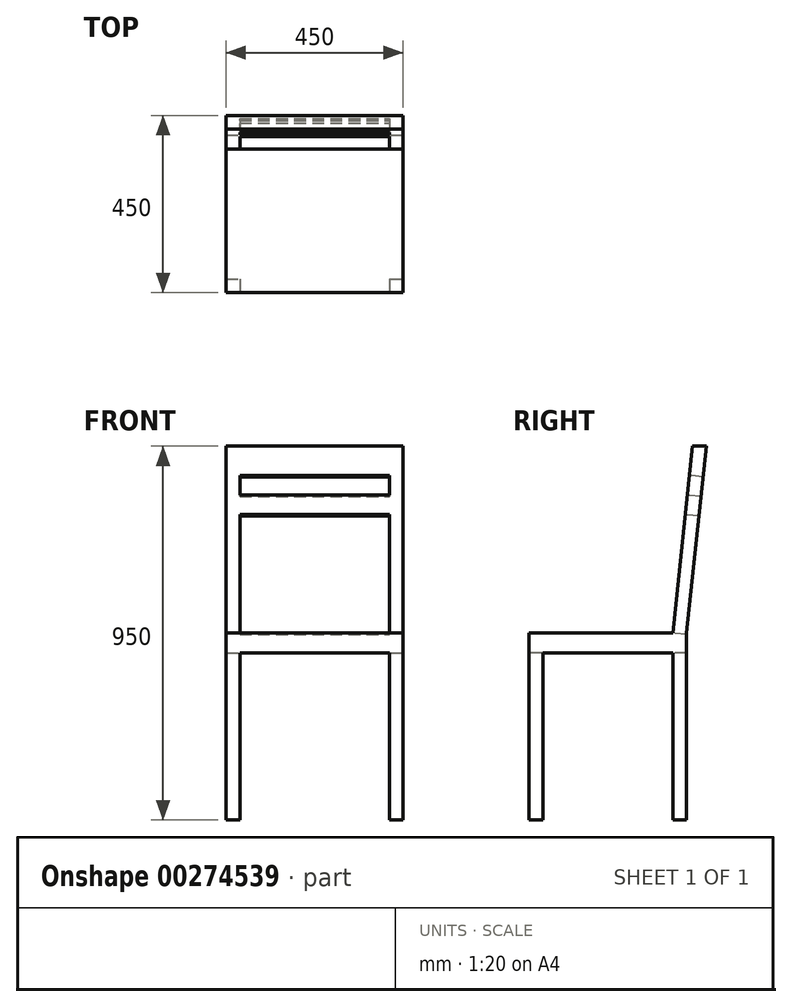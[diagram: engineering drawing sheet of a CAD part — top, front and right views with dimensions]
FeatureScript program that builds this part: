
annotation { "Feature Type Name" : "Feature", "Feature Type Description" : "" }
export const myFeature = defineFeature(function(context is Context, id is Id, definition is map)
    precondition{}
    {
        {
            var Q0;
            Q0=qCreatedBy(makeId("Top.planeOp"),FACE);
            var sketch = newSketch(context, id + "F0", { "sketchPlane" : qUnion([Q0])});
            skLineSegment(sketch, "E0.bottom", {"start": v(225, 225) * mm, "end": v(-225, 225) * mm});
            skLineSegment(sketch, "E0.top", {"start": v(225, -225) * mm, "end": v(-225, -225) * mm});
            skLineSegment(sketch, "E0.left", {"start": v(225, 225) * mm, "end": v(225, -225) * mm});
            skLineSegment(sketch, "E0.right", {"start": v(-225, 225) * mm, "end": v(-225, -225) * mm});
            skPoint(sketch, "E0.middle", {"position": v(0, 0) * mm});
            skSolve(sketch);
        }
        {
            var Q0;
            Q0=qSketchRegion(id+"F0",true);
            extrude(context, id + "F1", {"entities" : qUnion([Q0]), "depth" : 950 * mm});
        }
        {
            var Q0;
            Q0=makeQuery(id+"F1.opExtrude","SWEPT_FACE",FACE,{"disambiguationData":[OSD([sQuery(id+"F0.wireOp",EDGE,"E0.left")])]});
            var sketch = newSketch(context, id + "F2", { "sketchPlane" : qUnion([Q0])});
            skLineSegment(sketch, "E1.bottom", {"start": v(225, 475) * mm, "end": v(-225, 475) * mm});
            skLineSegment(sketch, "E1.top", {"start": v(225, 425) * mm, "end": v(-225, 425) * mm});
            skLineSegment(sketch, "E1.left", {"start": v(225, 475) * mm, "end": v(225, 425) * mm});
            skLineSegment(sketch, "E1.right", {"start": v(-225, 475) * mm, "end": v(-225, 425) * mm});
            skLineSegment(sketch, "E2", {"start": v(225, 950) * mm, "end": v(175, 475) * mm});
            skLineSegment(sketch, "E3", {"start": v(190, 950) * mm, "end": v(140, 475) * mm});
            skLineSegment(sketch, "E4", {"start": v(175, 475) * mm, "end": v(175, 0) * mm});
            skLineSegment(sketch, "E5", {"start": v(140, 475) * mm, "end": v(140, -16.84) * mm});
            skLineSegment(sketch, "E6.bottom", {"start": v(-225, 0) * mm, "end": v(-190, 0) * mm});
            skLineSegment(sketch, "E6.top", {"start": v(-225, 425) * mm, "end": v(-190, 425) * mm});
            skLineSegment(sketch, "E6.left", {"start": v(-225, 0) * mm, "end": v(-225, 425) * mm});
            skLineSegment(sketch, "E6.right", {"start": v(-190, 0) * mm, "end": v(-190, 425) * mm});
            skSolve(sketch);
        }
        {
            var Q0;
            {var subQ4=sQuery(id+"F2.wireOp",EDGE,"E3");Q0=makeQuery(id+"F2.imprint","IMPRINT",FACE,{"disambiguationData":[TD([[makeQuery(id+"F2.imprint","IMPRINT",EDGE,{"derivedFrom":subQ4}),-1.0]])]});}
            var Q1;
            {var subQ0=sQuery(id+"F2.wireOp",EDGE,"E6.right");Q1=makeQuery(id+"F2.imprint","IMPRINT",FACE,{"disambiguationData":[TD([[makeQuery(id+"F2.imprint","IMPRINT",EDGE,{"derivedFrom":subQ0}),-1.0]])]});}
            var Q2;
            {var subQ1=sQuery(id+"F0.wireOp",EDGE,"E0.left");var subQ4=sQuery(id+"F2.wireOp",EDGE,"E4");var subQ6=makeQuery(id+"F1.opExtrude","CAP_EDGE",EDGE,{"disambiguationData":[OSD([subQ1])],"isStart":true});var subQ7=makeQuery(id+"F2.imprint","INTERSECT",VERTEX,{"derivedFrom":[subQ6,subQ4]});Q2=makeQuery(id+"F2.imprint","IMPRINT",FACE,{"disambiguationData":[TD([[makeQuery(id+"F2.imprint","IMPRINT",EDGE,{"disambiguationData":[TD([[subQ7,1.0]])],"derivedFrom":subQ4}),1.0]])]});}
            var Q3;
            {var subQ4=sQuery(id+"F2.wireOp",EDGE,"E2");Q3=makeQuery(id+"F2.imprint","IMPRINT",FACE,{"disambiguationData":[TD([[makeQuery(id+"F2.imprint","IMPRINT",EDGE,{"derivedFrom":subQ4}),1.0]])]});}
            var Q4;
            {var subQ0=sQuery(id+"F2.wireOp",EDGE,"E1.left");Q4=makeQuery(id+"F2.imprint","IMPRINT",FACE,{"disambiguationData":[TD([[makeQuery(id+"F2.imprint","IMPRINT",EDGE,{"derivedFrom":subQ0}),-1.0]])]});}
            extrude(context, id + "F3", {"entities" : qUnion([Q0, Q1, Q2, Q3, Q4]), "operationType" : NewBodyOperationType.REMOVE, "endBound" : BoundingType.THROUGH_ALL, "oppositeDirection" : true, "depth" : 25 * mm});
        }
        {
            var Q0;
            Q0=makeQuery(id+"F1.opExtrude","SWEPT_FACE",FACE,{"disambiguationData":[OSD([sQuery(id+"F0.wireOp",EDGE,"E0.top")])]});
            var sketch = newSketch(context, id + "F4", { "sketchPlane" : qUnion([Q0])});
            skLineSegment(sketch, "E7", {"start": v(-190, 0) * mm, "end": v(-190, 425) * mm});
            skLineSegment(sketch, "E8", {"start": v(-190, 425) * mm, "end": v(190, 425) * mm});
            skLineSegment(sketch, "E9", {"start": v(190, 425) * mm, "end": v(190, 0) * mm});
            skSolve(sketch);
        }
        {
            var Q0;
            Q0 = qSketchRegion(id + "F4", true);
            var Q1;
            {var subQ0=sQuery(id+"F4.wireOp",EDGE,"E7");Q1=makeQuery(id+"F4.imprint","IMPRINT",FACE,{"disambiguationData":[TD([[makeQuery(id+"F4.imprint","IMPRINT",EDGE,{"derivedFrom":subQ0}),-1.0]])]});}
            extrude(context, id + "F5", {"entities" : qUnion([Q0, Q1]), "operationType" : NewBodyOperationType.REMOVE, "endBound" : BoundingType.THROUGH_ALL, "oppositeDirection" : true, "depth" : 25 * mm});
        }
        {
            var Q0;
            Q0=makeQuery(id+"F3.boolean.opBoolean","COPY",FACE,{"derivedFrom":makeQuery(id+"F3.opExtrude","SWEPT_FACE",FACE,{"disambiguationData":[OSD([sQuery(id+"F2.wireOp",EDGE,"E3")])]})});
            var sketch = newSketch(context, id + "F6", { "sketchPlane" : qUnion([Q0])});
            skLineSegment(sketch, "E10", {"start": v(-190, 487.05) * mm, "end": v(-190, 889.67) * mm});
            skLineSegment(sketch, "E11", {"start": v(-190, 889.67) * mm, "end": v(190, 889.67) * mm});
            skLineSegment(sketch, "E12", {"start": v(190, 889.67) * mm, "end": v(190, 487.05) * mm});
            skLineSegment(sketch, "E13", {"start": v(-190, 839.67) * mm, "end": v(190, 839.67) * mm});
            skLineSegment(sketch, "E14", {"start": v(-190, 789.67) * mm, "end": v(190, 789.67) * mm});
            skSolve(sketch);
        }
        {
            var Q0;
            {var subQ0=sQuery(id+"F6.wireOp",EDGE,"E11");Q0=makeQuery(id+"F6.imprint","IMPRINT",FACE,{"disambiguationData":[TD([[makeQuery(id+"F6.imprint","IMPRINT",EDGE,{"derivedFrom":subQ0}),-1.0]])]});}
            var Q1;
            {var subQ3=sQuery(id+"F6.wireOp",EDGE,"E14");Q1=makeQuery(id+"F6.imprint","IMPRINT",FACE,{"disambiguationData":[TD([[makeQuery(id+"F6.imprint","IMPRINT",EDGE,{"derivedFrom":subQ3}),-1.0]])]});}
            extrude(context, id + "F7", {"entities" : qUnion([Q0, Q1]), "operationType" : NewBodyOperationType.REMOVE, "endBound" : BoundingType.THROUGH_ALL, "oppositeDirection" : true, "depth" : 25 * mm});
        }
    });
